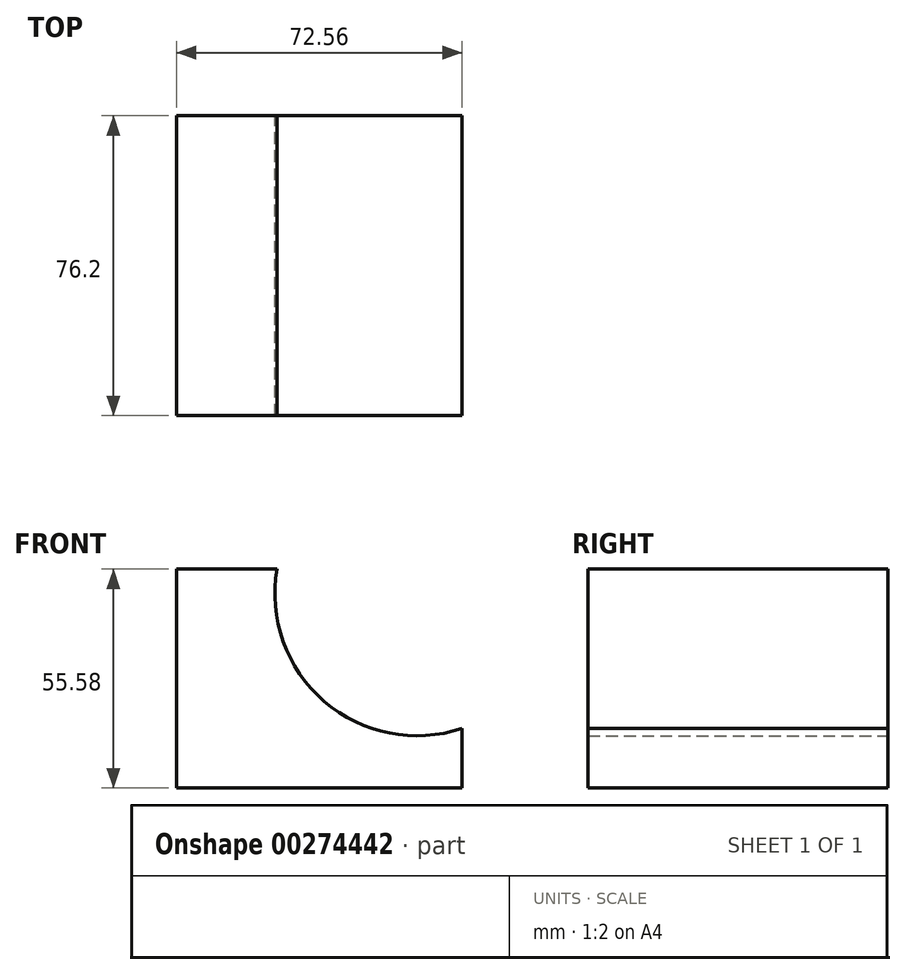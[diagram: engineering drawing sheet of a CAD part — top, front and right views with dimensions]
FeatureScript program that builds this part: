
annotation { "Feature Type Name" : "Feature", "Feature Type Description" : "" }
export const myFeature = defineFeature(function(context is Context, id is Id, definition is map)
    precondition{}
    {
        {
            var Q0;
            Q0=qCreatedBy(makeId("Front.planeOp"),FACE);
            var sketch = newSketch(context, id + "F0", { "sketchPlane" : qUnion([Q0])});
            skLineSegment(sketch, "E0", {"start": v(0, 0) * mm, "end": v(-72.56, 0) * mm});
            skLineSegment(sketch, "E1", {"start": v(-72.56, 0) * mm, "end": v(-72.56, 55.58) * mm});
            skLineSegment(sketch, "E2", {"start": v(-72.56, 55.58) * mm, "end": v(-51.36, 55.58) * mm});
            skLineSegment(sketch, "E3", {"start": v(-51.36, 55.58) * mm, "end": v(-46.97, 55.58) * mm});
            skLineSegment(sketch, "E4", {"start": v(0, 0) * mm, "end": v(0, 15.09) * mm});
            skArc(sketch, "E5", {"start": v(-46.97, 55.58) * mm, "mid": v(-35, 21.97) * mm, "end": v(0, 15.09) * mm});
            skSolve(sketch);
        }
        {
            var Q0;
            Q0 = qSketchRegion(id + "F0", true);
            extrude(context, id + "F1", {"entities" : qUnion([Q0]), "depth" : 76.2 * mm});
        }
    });
